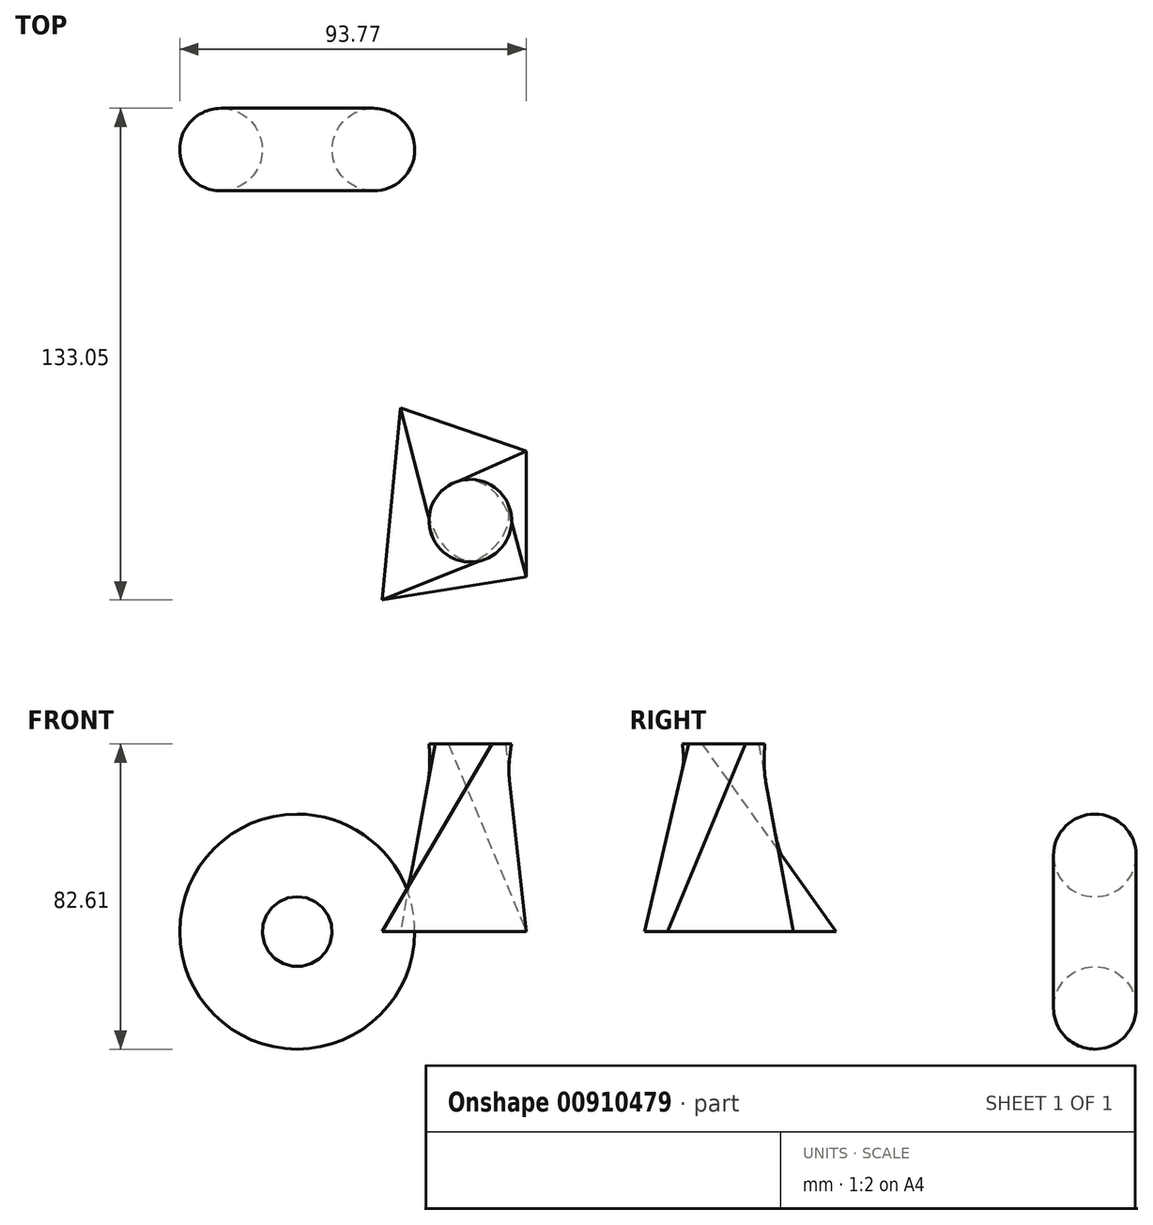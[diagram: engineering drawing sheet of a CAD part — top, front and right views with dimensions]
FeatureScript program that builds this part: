
annotation { "Feature Type Name" : "Feature", "Feature Type Description" : "" }
export const myFeature = defineFeature(function(context is Context, id is Id, definition is map)
    precondition{}
    {
        {
            var Q0;
            Q0=qCreatedBy(makeId("Top.planeOp"),FACE);
            var sketch = newSketch(context, id + "F0", { "sketchPlane" : qUnion([Q0])});
            skCircle(sketch, "E0", {"center": v(-62.28, 52.52) * mm, "radius": 11.18 * mm});
            skLineSegment(sketch, "E1.bottom", {"start": v(23.25, 37.16) * mm, "end": v(59.79, 37.16) * mm});
            skLineSegment(sketch, "E1.top", {"start": v(23.25, 15.57) * mm, "end": v(59.79, 15.57) * mm});
            skLineSegment(sketch, "E1.left", {"start": v(23.25, 37.16) * mm, "end": v(23.25, 15.57) * mm});
            skLineSegment(sketch, "E1.right", {"start": v(59.79, 37.16) * mm, "end": v(59.79, 15.57) * mm});
            skLineSegment(sketch, "E2", {"start": v(-55, -17.45) * mm, "end": v(-20.95, -29.08) * mm});
            skLineSegment(sketch, "E3", {"start": v(-20.95, -29.08) * mm, "end": v(-20.95, -63.13) * mm});
            skLineSegment(sketch, "E4", {"start": v(-20.95, -63.13) * mm, "end": v(-59.98, -69.35) * mm});
            skLineSegment(sketch, "E5", {"start": v(-59.98, -69.35) * mm, "end": v(-55, -17.45) * mm});
            skLineSegment(sketch, "E6", {"start": v(-82.91, 71.7) * mm, "end": v(-82.91, 30.26) * mm, "construction": true});
            skSolve(sketch);
        }
        {
            var Q0;
            Q0=qCreatedBy(makeId("Top.planeOp"),FACE);
            cPlane(context, id + "F1", {"entities" : qUnion([Q0]), "cplaneType" : CPlaneType.OFFSET, "offset" : 50.8 * mm, "width" : 152.4 * mm, "height" : 152.4 * mm});
        }
        {
            var Q0;
            Q0=qCreatedBy(id+"F1.planeOp",FACE);
            var sketch = newSketch(context, id + "F2", { "sketchPlane" : qUnion([Q0])});
            skCircle(sketch, "E7.0", {"center": v(-36.07, -47.94) * mm, "radius": 11.18 * mm});
            skLineSegment(sketch, "E7.1.0", {"start": v(-65.53, 33.82) * mm, "end": v(-46.83, 44.61) * mm});
            skLineSegment(sketch, "E7.1.1", {"start": v(-46.83, 44.61) * mm, "end": v(-65.1, 76.26) * mm});
            skLineSegment(sketch, "E7.1.2", {"start": v(-65.1, 76.26) * mm, "end": v(-83.8, 65.46) * mm});
            skLineSegment(sketch, "E7.1.3", {"start": v(-83.8, 65.46) * mm, "end": v(-65.53, 33.82) * mm});
            skLineSegment(sketch, "E7.2.0", {"start": v(20.9, -6.64) * mm, "end": v(68.33, 15) * mm});
            skLineSegment(sketch, "E7.2.1", {"start": v(68.33, 15) * mm, "end": v(43.42, 45.68) * mm});
            skLineSegment(sketch, "E7.2.2", {"start": v(43.42, 45.68) * mm, "end": v(13.94, 28.66) * mm});
            skLineSegment(sketch, "E7.2.3", {"start": v(13.94, 28.66) * mm, "end": v(20.9, -6.64) * mm});
            skSolve(sketch);
        }
        {
            var Q0;
            Q0=makeQuery(id+"F2.imprint","IMPRINT",FACE,{"disambiguationData":[TD([[makeQuery(id+"F2.imprint","IMPRINT",EDGE,{"derivedFrom":sQuery(id+"F2.wireOp",EDGE,"E7.0")}),1.0]])]});
            var Q1;
            Q1=makeQuery(id+"F0.imprint","IMPRINT",FACE,{"disambiguationData":[TD([[makeQuery(id+"F0.imprint","IMPRINT",EDGE,{"derivedFrom":sQuery(id+"F0.wireOp",EDGE,"E2")}),-1.0]])]});
            loft(context, id + "F3", {"sheetProfilesArray" : [{ "sheetProfileEntities" : qUnion([Q0]) }, { "sheetProfileEntities" : qUnion([Q1]) }]});
        }
        {
            var Q0;
            Q0=makeQuery(id+"F0.imprint","IMPRINT",FACE,{"disambiguationData":[TD([[makeQuery(id+"F0.imprint","IMPRINT",EDGE,{"derivedFrom":sQuery(id+"F0.wireOp",EDGE,"E0")}),1.0]])]});
            var Q1;
            Q1=sQuery(id+"F0.wireOp",EDGE,"E6");
            revolve(context, id + "F4", {"surfaceOperationType" : NewSurfaceOperationType.NEW, "entities" : qUnion([Q0]), "axis" : qUnion([Q1]), "revolveType" : RevolveType.FULL});
        }
    });
